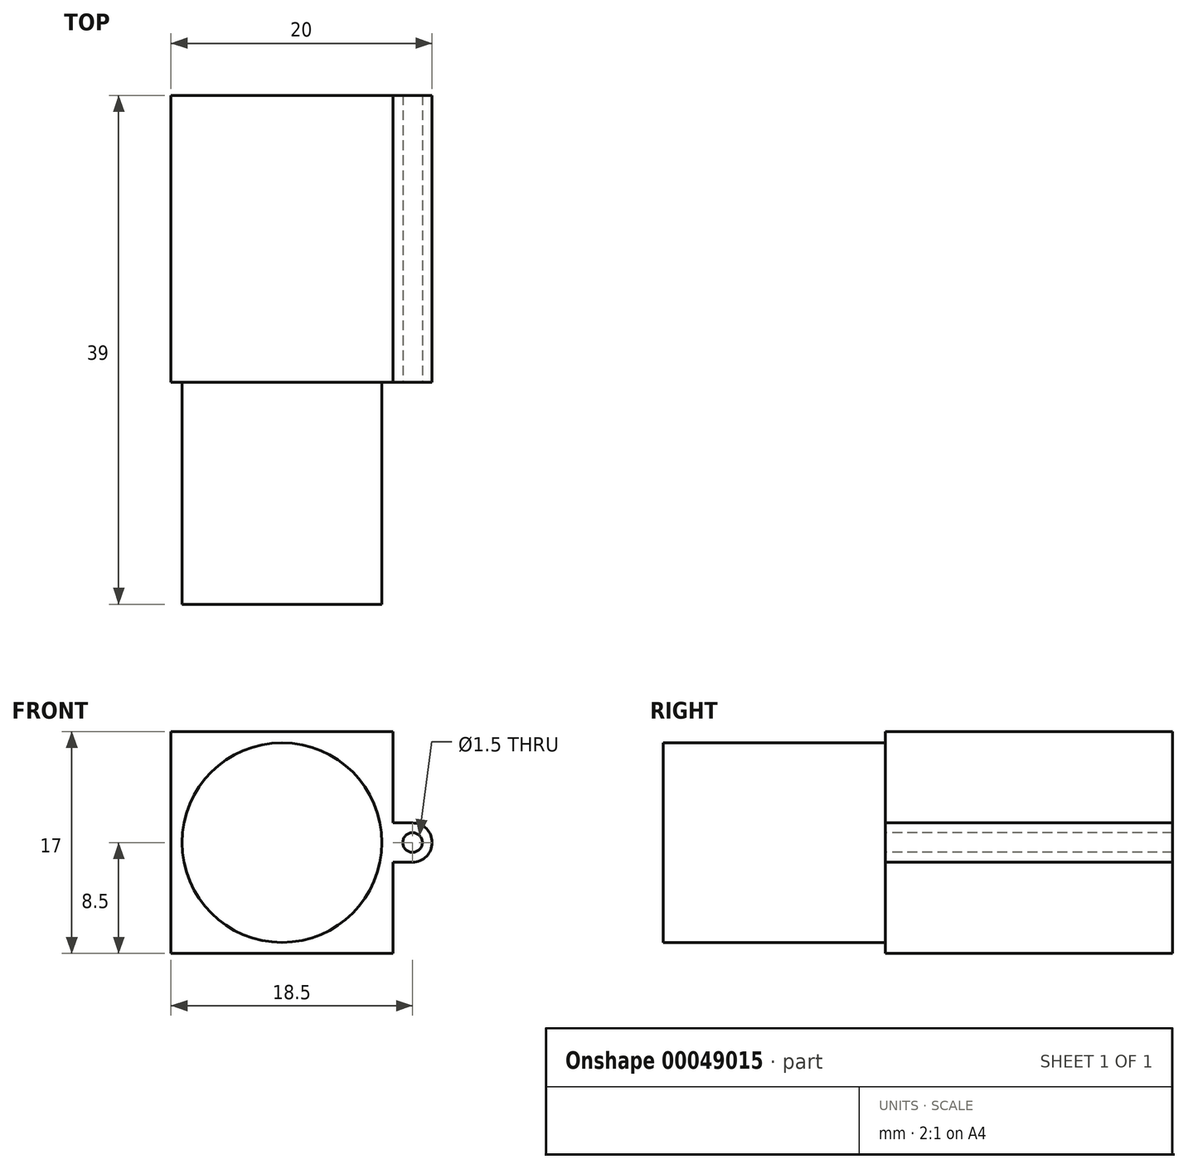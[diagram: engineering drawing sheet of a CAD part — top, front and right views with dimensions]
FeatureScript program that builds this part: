
annotation { "Feature Type Name" : "Feature", "Feature Type Description" : "" }
export const myFeature = defineFeature(function(context is Context, id is Id, definition is map)
    precondition{}
    {
        {
            var Q0;
            Q0=qCreatedBy(makeId("Front.planeOp"),FACE);
            var sketch = newSketch(context, id + "F0", { "sketchPlane" : qUnion([Q0])});
            skCircle(sketch, "E0", {"center": v(0, 0) * mm, "radius": 7.65 * mm});
            skSolve(sketch);
        }
        {
            var Q0;
            Q0 = qSketchRegion(id + "F0", true);
            extrude(context, id + "F1", {"entities" : qUnion([Q0]), "depth" : 17 * mm});
        }
        {
            var Q0;
            Q0=qCreatedBy(makeId("Front.planeOp"),FACE);
            var sketch = newSketch(context, id + "F2", { "sketchPlane" : qUnion([Q0])});
            skLineSegment(sketch, "E1.bottom", {"start": v(8.5, 8.5) * mm, "end": v(-8.5, 8.5) * mm});
            skLineSegment(sketch, "E1.top", {"start": v(8.5, -8.5) * mm, "end": v(-8.5, -8.5) * mm});
            skLineSegment(sketch, "E1.left", {"start": v(8.5, 8.5) * mm, "end": v(8.5, -8.5) * mm});
            skLineSegment(sketch, "E1.right", {"start": v(-8.5, 8.5) * mm, "end": v(-8.5, -8.5) * mm});
            skPoint(sketch, "E1.middle", {"position": v(0, 0) * mm});
            skSolve(sketch);
        }
        {
            var Q0;
            Q0 = qSketchRegion(id + "F2", true);
            extrude(context, id + "F3", {"entities" : qUnion([Q0]), "operationType" : NewBodyOperationType.ADD, "oppositeDirection" : true, "depth" : 22 * mm});
        }
        {
            var Q0;
            Q0=qCreatedBy(makeId("Front.planeOp"),FACE);
            var sketch = newSketch(context, id + "F4", { "sketchPlane" : qUnion([Q0])});
            skLineSegment(sketch, "E2", {"start": v(0, 0) * mm, "end": v(8.5, 0) * mm, "construction": true});
            skLineSegment(sketch, "E3", {"start": v(8.5, 0) * mm, "end": v(10, 0) * mm, "construction": true});
            skCircle(sketch, "E4", {"center": v(10, 0) * mm, "radius": 0.75 * mm});
            skCircle(sketch, "E5", {"center": v(10, 0) * mm, "radius": 1.5 * mm});
            skLineSegment(sketch, "E6.bottom", {"start": v(10, 1.5) * mm, "end": v(8.5, 1.5) * mm});
            skLineSegment(sketch, "E6.top", {"start": v(10, -1.5) * mm, "end": v(8.5, -1.5) * mm});
            skLineSegment(sketch, "E6.right", {"start": v(8.5, 1.5) * mm, "end": v(8.5, -1.5) * mm});
            skSolve(sketch);
        }
        {
            var Q0;
            Q0 = qSketchRegion(id + "F4", true);
            extrude(context, id + "F5", {"entities" : qUnion([Q0]), "operationType" : NewBodyOperationType.ADD, "oppositeDirection" : true, "depth" : 22 * mm});
        }
    });
